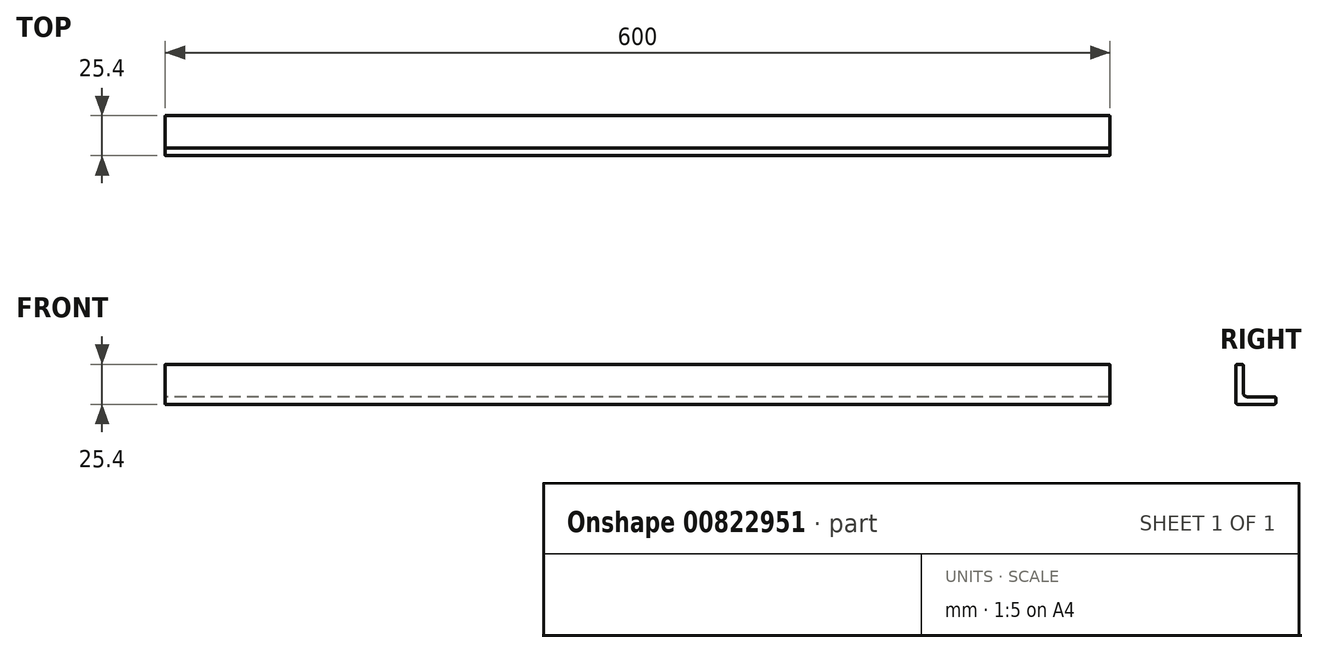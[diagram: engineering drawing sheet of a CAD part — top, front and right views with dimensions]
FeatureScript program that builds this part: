
annotation { "Feature Type Name" : "Feature", "Feature Type Description" : "" }
export const myFeature = defineFeature(function(context is Context, id is Id, definition is map)
    precondition{}
    {
        {
            var Q0;
            Q0=qCreatedBy(makeId("Right.planeOp"),FACE);
            var sketch = newSketch(context, id + "F0", { "sketchPlane" : qUnion([Q0])});
            skLineSegment(sketch, "E0", {"start": v(0, 0) * mm, "end": v(25.4, 0) * mm});
            skLineSegment(sketch, "E1", {"start": v(0, 0) * mm, "end": v(0, 25.4) * mm});
            skLineSegment(sketch, "E2", {"start": v(0, 25.4) * mm, "end": v(4.76, 25.4) * mm});
            skLineSegment(sketch, "E3", {"start": v(4.76, 25.4) * mm, "end": v(4.76, 4.76) * mm});
            skLineSegment(sketch, "E4", {"start": v(4.76, 4.76) * mm, "end": v(25.4, 4.76) * mm});
            skLineSegment(sketch, "E5", {"start": v(25.4, 4.76) * mm, "end": v(25.4, 0) * mm});
            skSolve(sketch);
        }
        {
            var Q0;
            Q0=qSketchRegion(id+"F0",true);
            extrude(context, id + "F1", {"entities" : qUnion([Q0]), "endBound" : BoundingType.SYMMETRIC, "depth" : 600 * mm, "offsetDistance" : 25 * mm});
        }
        {
            var Q0;
            Q0=makeQuery(id+"F1.opExtrude","SWEPT_EDGE",EDGE,{"disambiguationData":[OSD([sQuery(id+"F0.wireOp",EDGE,"E1"),sQuery(id+"F0.wireOp",EDGE,"E2")])]});
            var Q1;
            Q1=makeQuery(id+"F1.opExtrude","SWEPT_EDGE",EDGE,{"disambiguationData":[OSD([sQuery(id+"F0.wireOp",EDGE,"E2"),sQuery(id+"F0.wireOp",EDGE,"E3")])]});
            var Q2;
            Q2=makeQuery(id+"F1.opExtrude","SWEPT_EDGE",EDGE,{"disambiguationData":[OSD([sQuery(id+"F0.wireOp",EDGE,"E0"),sQuery(id+"F0.wireOp",EDGE,"E1")])]});
            var Q3;
            Q3=makeQuery(id+"F1.opExtrude","SWEPT_EDGE",EDGE,{"disambiguationData":[OSD([sQuery(id+"F0.wireOp",EDGE,"E4"),sQuery(id+"F0.wireOp",EDGE,"E5")])]});
            var Q4;
            Q4=makeQuery(id+"F1.opExtrude","SWEPT_EDGE",EDGE,{"disambiguationData":[OSD([sQuery(id+"F0.wireOp",EDGE,"E0"),sQuery(id+"F0.wireOp",EDGE,"E5")])]});
            fillet(context, id + "F2", {"entities" : qUnion([Q0, Q1, Q2, Q3, Q4]), "radius" : 1 * mm, "tangentPropagation" : true, "allowEdgeOverflow" : false});
        }
        {
            var Q0;
            Q0=makeQuery(id+"F1.opExtrude","SWEPT_EDGE",EDGE,{"disambiguationData":[OSD([sQuery(id+"F0.wireOp",EDGE,"E3"),sQuery(id+"F0.wireOp",EDGE,"E4")])]});
            fillet(context, id + "F3", {"entities" : qUnion([Q0]), "radius" : (3 * 25.4 / 16 / 2) * mm, "tangentPropagation" : true, "allowEdgeOverflow" : false});
        }
    });
